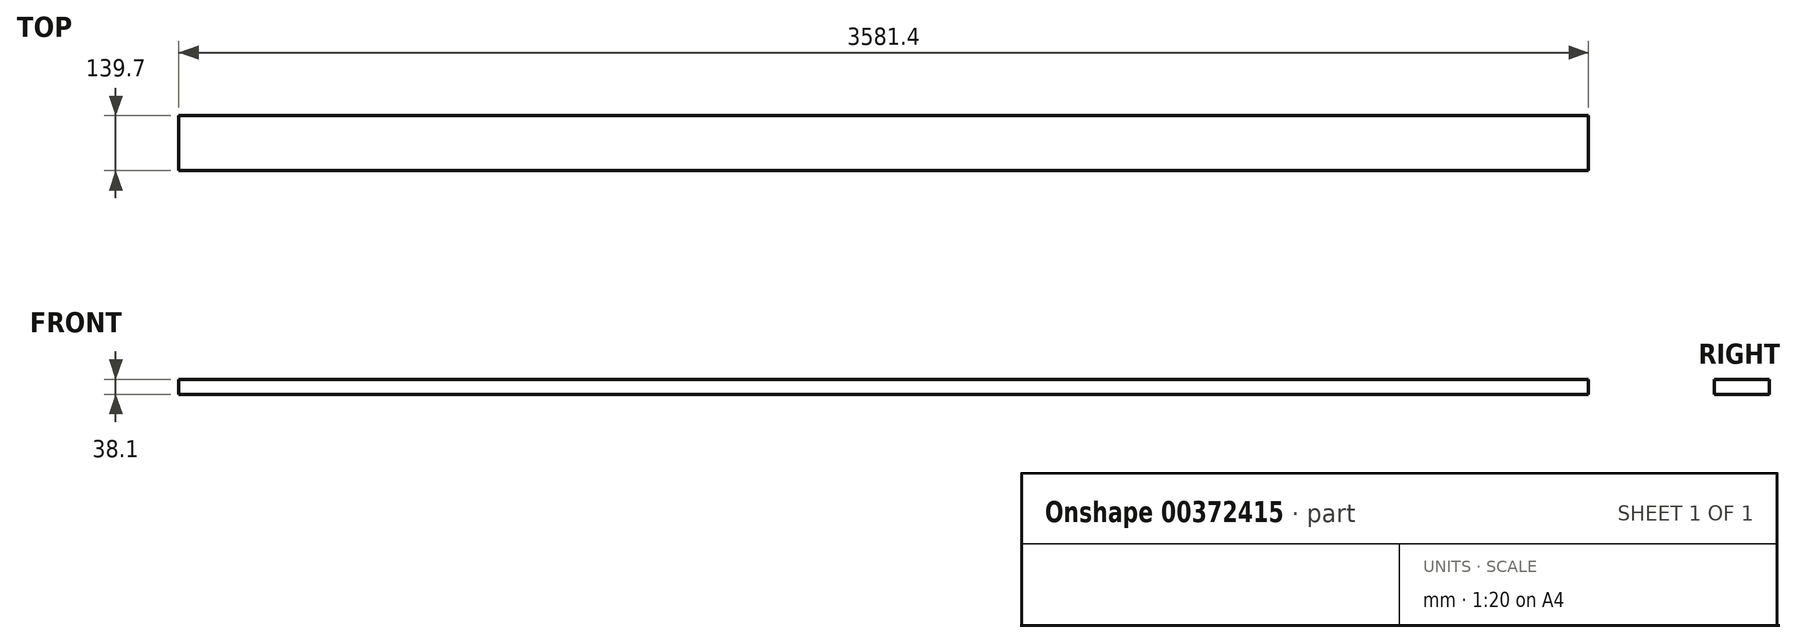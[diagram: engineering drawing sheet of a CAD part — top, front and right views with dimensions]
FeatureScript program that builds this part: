
annotation { "Feature Type Name" : "Feature", "Feature Type Description" : "" }
export const myFeature = defineFeature(function(context is Context, id is Id, definition is map)
    precondition{}
    {
        {
            var Q0;
            Q0=qCreatedBy(makeId("Top.planeOp"),FACE);
            var sketch = newSketch(context, id + "F0", { "sketchPlane" : qUnion([Q0])});
            skLineSegment(sketch, "E0.bottom", {"start": v(1790.7, -69.85) * mm, "end": v(-1790.7, -69.85) * mm});
            skLineSegment(sketch, "E0.top", {"start": v(1790.7, 69.85) * mm, "end": v(-1790.7, 69.85) * mm});
            skLineSegment(sketch, "E0.left", {"start": v(1790.7, -69.85) * mm, "end": v(1790.7, 69.85) * mm});
            skLineSegment(sketch, "E0.right", {"start": v(-1790.7, -69.85) * mm, "end": v(-1790.7, 69.85) * mm});
            skPoint(sketch, "E0.middle", {"position": v(0, 0) * mm});
            skSolve(sketch);
        }
        {
            var Q0;
            Q0=qSketchRegion(id+"F0",true);
            extrude(context, id + "F1", {"entities" : qUnion([Q0]), "oppositeDirection" : true, "depth" : 38.1 * mm});
        }
    });
